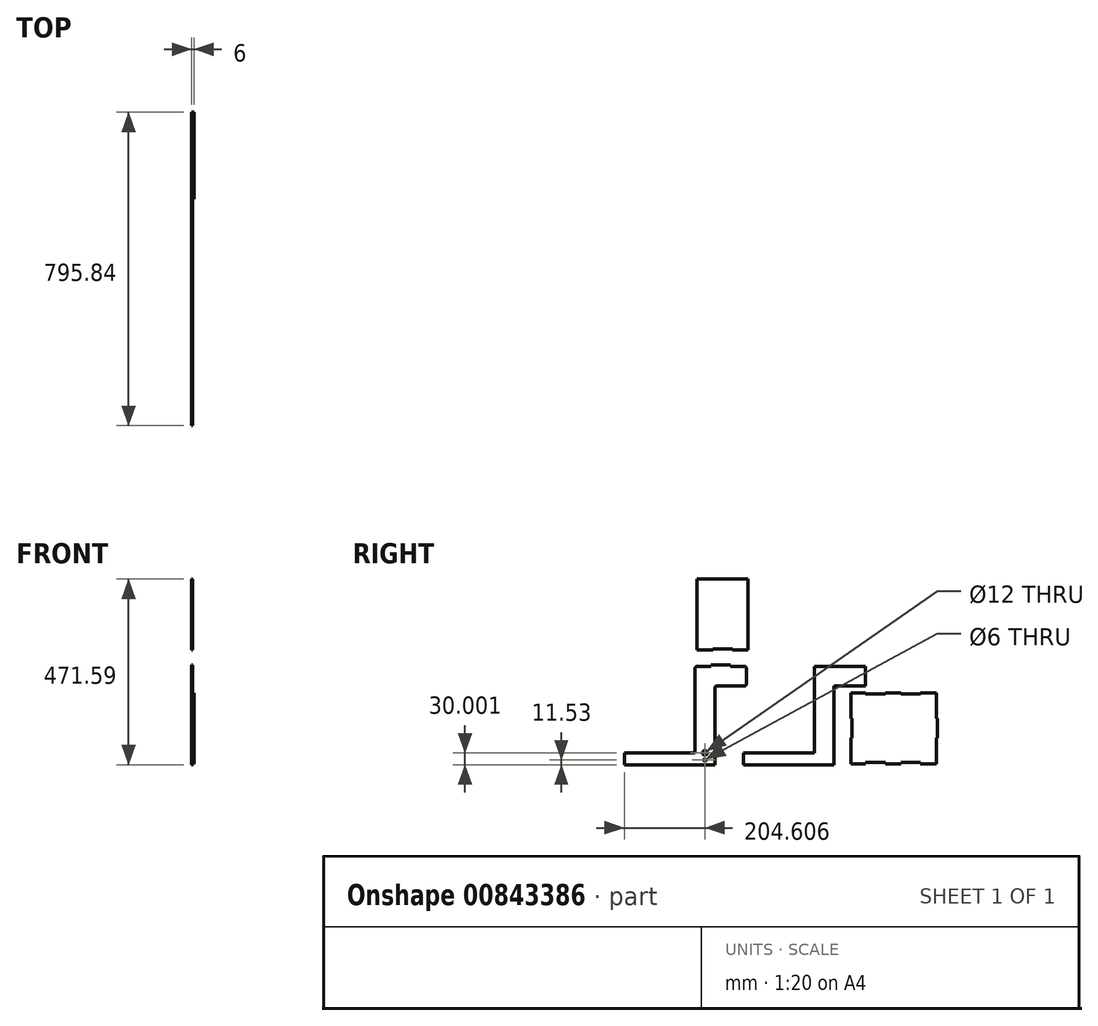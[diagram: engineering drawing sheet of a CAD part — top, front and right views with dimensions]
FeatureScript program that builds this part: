
annotation { "Feature Type Name" : "Feature", "Feature Type Description" : "" }
export const myFeature = defineFeature(function(context is Context, id is Id, definition is map)
    precondition{}
    {
        {
            var Q0;
            Q0=qCreatedBy(makeId("Right.planeOp"),FACE);
            var sketch = newSketch(context, id + "F0", { "sketchPlane" : qUnion([Q0])});
            skLineSegment(sketch, "E0", {"start": v(0, 42.16) * mm, "end": v(130, 42.16) * mm});
            skLineSegment(sketch, "E1", {"start": v(130, 42.16) * mm, "end": v(130, -7.84) * mm});
            skLineSegment(sketch, "E2", {"start": v(50, -7.84) * mm, "end": v(130, -7.84) * mm});
            skLineSegment(sketch, "E3", {"start": v(50, -7.84) * mm, "end": v(50, -207.84) * mm});
            skLineSegment(sketch, "E4", {"start": v(50, -207.84) * mm, "end": v(-180, -207.84) * mm});
            skLineSegment(sketch, "E5", {"start": v(-180, -207.84) * mm, "end": v(-180, -177.84) * mm});
            skLineSegment(sketch, "E6", {"start": v(0, -177.84) * mm, "end": v(-180, -177.84) * mm});
            skLineSegment(sketch, "E7", {"start": v(0, -177.84) * mm, "end": v(0, 42.16) * mm});
            skLineSegment(sketch, "E8", {"start": v(-298.05, 42.16) * mm, "end": v(-263.05, 42.16) * mm});
            skLineSegment(sketch, "E9", {"start": v(-173.05, 37.16) * mm, "end": v(-173.05, -2.84) * mm});
            skLineSegment(sketch, "E10", {"start": v(-248.05, -7.84) * mm, "end": v(-178.05, -7.84) * mm});
            skLineSegment(sketch, "E11", {"start": v(-253.05, -12.84) * mm, "end": v(-253.05, -207.84) * mm});
            skLineSegment(sketch, "E12", {"start": v(-253.05, -207.84) * mm, "end": v(-483.05, -207.84) * mm});
            skLineSegment(sketch, "E13", {"start": v(-483.05, -207.84) * mm, "end": v(-483.05, -177.84) * mm});
            skLineSegment(sketch, "E14", {"start": v(-303.05, -177.84) * mm, "end": v(-483.05, -177.84) * mm});
            skLineSegment(sketch, "E15", {"start": v(-303.05, -177.84) * mm, "end": v(-303.05, 37.16) * mm});
            skCircle(sketch, "E16", {"center": v(-278.44, -177.84) * mm, "radius": 6 * mm});
            skLineSegment(sketch, "E17.bottom", {"start": v(-298.36, 83.75) * mm, "end": v(-258.01, 83.75) * mm});
            skLineSegment(sketch, "E17.top", {"start": v(-298.36, 263.75) * mm, "end": v(-168.36, 263.75) * mm});
            skLineSegment(sketch, "E17.left", {"start": v(-298.36, 83.75) * mm, "end": v(-298.36, 263.75) * mm});
            skLineSegment(sketch, "E17.right", {"start": v(-168.36, 83.75) * mm, "end": v(-168.36, 263.75) * mm});
            skCircle(sketch, "E18", {"center": v(-278.44, -196.31) * mm, "radius": 3 * mm});
            skLineSegment(sketch, "E19", {"start": v(-263.05, 42.16) * mm, "end": v(-263.05, 45.16) * mm});
            skLineSegment(sketch, "E20", {"start": v(-263.05, 45.16) * mm, "end": v(-213.05, 45.16) * mm});
            skLineSegment(sketch, "E21", {"start": v(-213.05, 45.16) * mm, "end": v(-213.05, 42.16) * mm});
            skLineSegment(sketch, "E22.trimOffspring", {"start": v(-213.05, 42.16) * mm, "end": v(-178.05, 42.16) * mm});
            skLineSegment(sketch, "E23.top", {"start": v(-258.01, 86.75) * mm, "end": v(-208.01, 86.75) * mm});
            skLineSegment(sketch, "E23.left", {"start": v(-258.01, 83.75) * mm, "end": v(-258.01, 86.75) * mm});
            skLineSegment(sketch, "E23.right", {"start": v(-208.01, 83.75) * mm, "end": v(-208.01, 86.75) * mm});
            skLineSegment(sketch, "E24.trimOffspring", {"start": v(-208.01, 83.75) * mm, "end": v(-168.36, 83.75) * mm});
            skPoint(sketch, "E25.visualSharp", {"position": v(-303.05, 42.16) * mm});
            skArc(sketch, "E25.filletArc", {"start": v(-298.05, 42.16) * mm, "mid": v(-301.59, 40.7) * mm, "end": v(-303.05, 37.16) * mm});
            skPoint(sketch, "E26.visualSharp", {"position": v(-173.05, 42.16) * mm});
            skArc(sketch, "E26.filletArc", {"start": v(-173.05, 37.16) * mm, "mid": v(-174.52, 40.7) * mm, "end": v(-178.05, 42.16) * mm});
            skPoint(sketch, "E27.visualSharp", {"position": v(-173.05, -7.84) * mm});
            skArc(sketch, "E27.filletArc", {"start": v(-178.05, -7.84) * mm, "mid": v(-174.52, -6.37) * mm, "end": v(-173.05, -2.84) * mm});
            skPoint(sketch, "E28.visualSharp", {"position": v(-253.05, -7.84) * mm});
            skArc(sketch, "E28.filletArc", {"start": v(-248.05, -7.84) * mm, "mid": v(-251.59, -9.3) * mm, "end": v(-253.05, -12.84) * mm});
            skLineSegment(sketch, "E29.bottom", {"start": v(92.79, -25.36) * mm, "end": v(129.79, -25.36) * mm});
            skLineSegment(sketch, "E29.top", {"start": v(92.79, -205.36) * mm, "end": v(129.79, -205.36) * mm});
            skLineSegment(sketch, "E29.right", {"start": v(309.79, -25.36) * mm, "end": v(309.79, -90.36) * mm});
            skLineSegment(sketch, "E30.bottom", {"start": v(309.79, -90.36) * mm, "end": v(312.79, -90.36) * mm});
            skLineSegment(sketch, "E30.top", {"start": v(309.79, -140.36) * mm, "end": v(312.79, -140.36) * mm});
            skLineSegment(sketch, "E30.right", {"start": v(312.79, -90.36) * mm, "end": v(312.79, -140.36) * mm});
            skLineSegment(sketch, "E31.trimOffspring", {"start": v(309.79, -140.36) * mm, "end": v(309.79, -205.36) * mm});
            skLineSegment(sketch, "E32", {"start": v(92.79, -25.36) * mm, "end": v(92.79, -90.36) * mm});
            skPoint(sketch, "E33.top.start.orphan", {"position": v(89.79, -140.36) * mm});
            skLineSegment(sketch, "E34.bottom", {"start": v(92.79, -90.36) * mm, "end": v(95.79, -90.36) * mm});
            skLineSegment(sketch, "E34.top", {"start": v(92.79, -140.36) * mm, "end": v(95.79, -140.36) * mm});
            skLineSegment(sketch, "E34.right", {"start": v(95.79, -90.36) * mm, "end": v(95.79, -140.36) * mm});
            skPoint(sketch, "E33.right.end.orphan", {"position": v(92.79, -140.36) * mm});
            skLineSegment(sketch, "E35.trimOffspring", {"start": v(92.79, -140.36) * mm, "end": v(92.79, -205.36) * mm});
            skLineSegment(sketch, "E36", {"start": v(309.79, -25.36) * mm, "end": v(269.79, -25.36) * mm});
            skLineSegment(sketch, "E37.top", {"start": v(269.79, -28.36) * mm, "end": v(219.79, -28.36) * mm});
            skLineSegment(sketch, "E37.left", {"start": v(269.79, -25.36) * mm, "end": v(269.79, -28.36) * mm});
            skLineSegment(sketch, "E37.right", {"start": v(219.79, -25.36) * mm, "end": v(219.79, -28.36) * mm});
            skLineSegment(sketch, "E38", {"start": v(219.79, -25.36) * mm, "end": v(179.79, -25.36) * mm});
            skLineSegment(sketch, "E39.top", {"start": v(179.79, -28.36) * mm, "end": v(129.79, -28.36) * mm});
            skLineSegment(sketch, "E39.left", {"start": v(179.79, -25.36) * mm, "end": v(179.79, -28.36) * mm});
            skLineSegment(sketch, "E39.right", {"start": v(129.79, -25.36) * mm, "end": v(129.79, -28.36) * mm});
            skLineSegment(sketch, "E40", {"start": v(129.79, -25.36) * mm, "end": v(92.79, -25.36) * mm});
            skLineSegment(sketch, "E41", {"start": v(309.79, -205.36) * mm, "end": v(269.79, -205.36) * mm});
            skLineSegment(sketch, "E42.top", {"start": v(269.79, -202.36) * mm, "end": v(219.79, -202.36) * mm});
            skLineSegment(sketch, "E42.left", {"start": v(269.79, -205.36) * mm, "end": v(269.79, -202.36) * mm});
            skLineSegment(sketch, "E42.right", {"start": v(219.79, -205.36) * mm, "end": v(219.79, -202.36) * mm});
            skLineSegment(sketch, "E43", {"start": v(219.79, -205.36) * mm, "end": v(179.79, -205.36) * mm});
            skLineSegment(sketch, "E44.top", {"start": v(179.79, -202.36) * mm, "end": v(129.79, -202.36) * mm});
            skLineSegment(sketch, "E44.left", {"start": v(179.79, -205.36) * mm, "end": v(179.79, -202.36) * mm});
            skLineSegment(sketch, "E44.right", {"start": v(129.79, -205.36) * mm, "end": v(129.79, -202.36) * mm});
            skLineSegment(sketch, "E45", {"start": v(129.79, -205.36) * mm, "end": v(92.79, -205.36) * mm});
            skLineSegment(sketch, "E46.trimOffspring", {"start": v(179.79, -25.36) * mm, "end": v(219.79, -25.36) * mm});
            skLineSegment(sketch, "E47.trimOffspring", {"start": v(269.79, -25.36) * mm, "end": v(309.79, -25.36) * mm});
            skLineSegment(sketch, "E48.trimOffspring", {"start": v(269.79, -205.36) * mm, "end": v(309.79, -205.36) * mm});
            skLineSegment(sketch, "E49.trimOffspring", {"start": v(179.79, -205.36) * mm, "end": v(219.79, -205.36) * mm});
            skSolve(sketch);
        }
        {
            var Q0;
            Q0=makeQuery(id+"F0.imprint","IMPRINT",FACE,{"disambiguationData":[TD([[makeQuery(id+"F0.imprint","IMPRINT",EDGE,{"derivedFrom":sQuery(id+"F0.wireOp",EDGE,"E0")}),-1.0]])]});
            var Q1;
            Q1=makeQuery(id+"F0.imprint","IMPRINT",FACE,{"disambiguationData":[TD([[makeQuery(id+"F0.imprint","IMPRINT",EDGE,{"derivedFrom":sQuery(id+"F0.wireOp",EDGE,"E8")}),-1.0]])]});
            var Q2;
            Q2=makeQuery(id+"F0.imprint","IMPRINT",FACE,{"disambiguationData":[TD([[makeQuery(id+"F0.imprint","IMPRINT",EDGE,{"derivedFrom":sQuery(id+"F0.wireOp",EDGE,"E17.bottom")}),1.0]])]});
            var Q3;
            Q3=makeQuery(id+"F0.imprint","IMPRINT",FACE,{"disambiguationData":[TD([[makeQuery(id+"F0.imprint","IMPRINT",EDGE,{"derivedFrom":sQuery(id+"F0.wireOp",EDGE,"E29.bottom")}),-1.0]])]});
            extrude(context, id + "F1", {"entities" : qUnion([Q0, Q1, Q2, Q3]), "oppositeDirection" : true, "depth" : 3 * mm, "offsetDistance" : 25 * mm});
        }
        {
            var Q0;
            Q0=makeQuery(id+"F0.imprint","IMPRINT",FACE,{"disambiguationData":[TD([[makeQuery(id+"F0.imprint","IMPRINT",EDGE,{"derivedFrom":sQuery(id+"F0.wireOp",EDGE,"E29.right")}),-1.0]])]});
            extrude(context, id + "F2", {"entities" : qUnion([Q0]), "depth" : 3 * mm, "offsetDistance" : 25 * mm});
        }
        {
            var Q0;
            Q0=makeQuery(id+"F2.opExtrude","SWEPT_BODY",BODY,{"disambiguationData":[OSD([sQuery(id+"F0.wireOp",EDGE,"E29.right"),sQuery(id+"F0.wireOp",EDGE,"E30.bottom"),sQuery(id+"F0.wireOp",EDGE,"E30.top"),sQuery(id+"F0.wireOp",EDGE,"E30.right"),sQuery(id+"F0.wireOp",EDGE,"E31.trimOffspring"),sQuery(id+"F0.wireOp",EDGE,"E32"),sQuery(id+"F0.wireOp",EDGE,"E34.bottom"),sQuery(id+"F0.wireOp",EDGE,"E34.top"),sQuery(id+"F0.wireOp",EDGE,"E34.right"),sQuery(id+"F0.wireOp",EDGE,"E35.trimOffspring"),sQuery(id+"F0.wireOp",EDGE,"E37.top"),sQuery(id+"F0.wireOp",EDGE,"E37.left"),sQuery(id+"F0.wireOp",EDGE,"E37.right"),sQuery(id+"F0.wireOp",EDGE,"E39.top"),sQuery(id+"F0.wireOp",EDGE,"E39.left"),sQuery(id+"F0.wireOp",EDGE,"E39.right"),sQuery(id+"F0.wireOp",EDGE,"E40"),sQuery(id+"F0.wireOp",EDGE,"E42.top"),sQuery(id+"F0.wireOp",EDGE,"E42.left"),sQuery(id+"F0.wireOp",EDGE,"E42.right"),sQuery(id+"F0.wireOp",EDGE,"E44.top"),sQuery(id+"F0.wireOp",EDGE,"E44.left"),sQuery(id+"F0.wireOp",EDGE,"E44.right"),sQuery(id+"F0.wireOp",EDGE,"E45"),sQuery(id+"F0.wireOp",EDGE,"E46.trimOffspring"),sQuery(id+"F0.wireOp",EDGE,"E47.trimOffspring"),sQuery(id+"F0.wireOp",EDGE,"E48.trimOffspring"),sQuery(id+"F0.wireOp",EDGE,"E49.trimOffspring")])]});
            transform(context, id + "F3", {"entities" : qUnion([Q0]), "transformType" : TransformType.TRANSLATION_3D, "dx" : 0 * mm, "dy" : 0 * mm, "dz" : 0 * mm, "makeCopy" : true});
        }
    });
